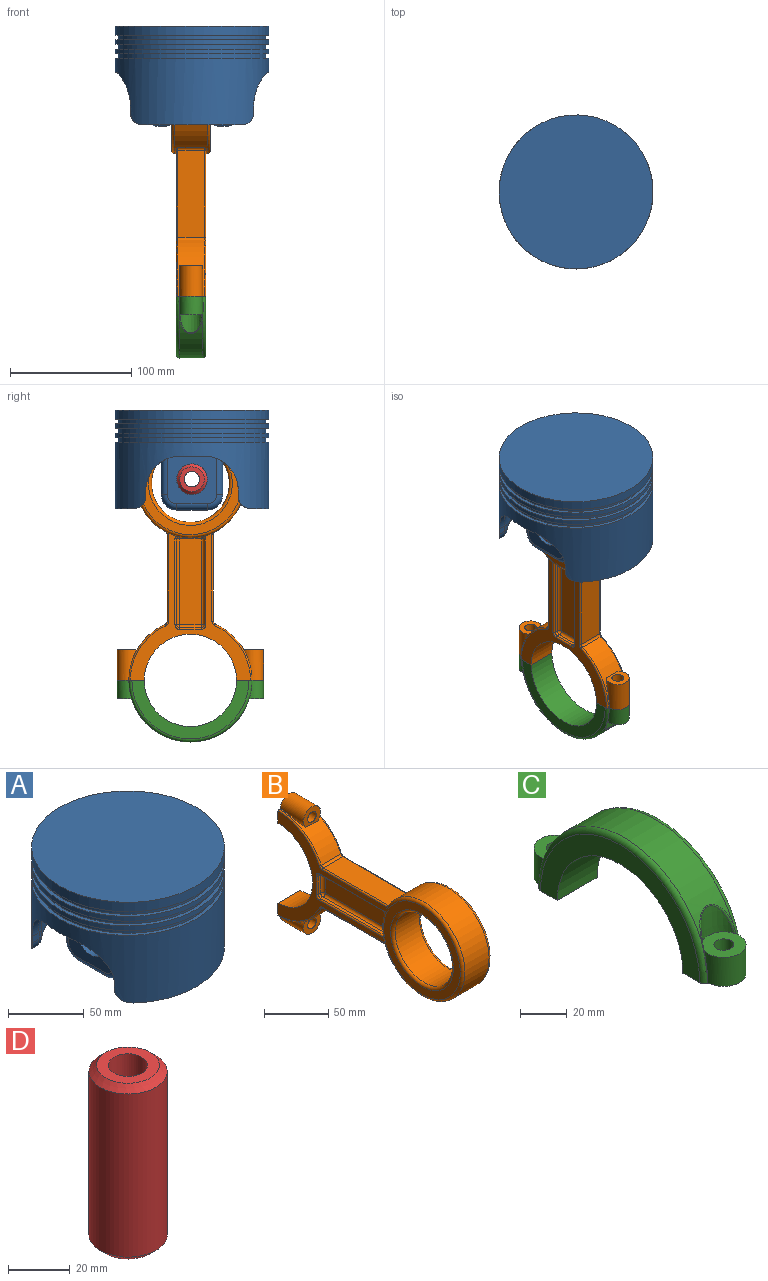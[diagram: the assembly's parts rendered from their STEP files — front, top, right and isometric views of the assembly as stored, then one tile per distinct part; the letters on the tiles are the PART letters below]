
ASSEMBLY  parts=4 mates=7
PART A: 84 faces, bbox 133.2x142.2x83.5 mm
  f0: plane 114.3x114.3mm, normal (0,0,-1), area 8373.3mm2, adj f1,f28,f29,f30,f31,f33,f34,f35
  f1: cylinder r=57.15mm len=114.3mm, axis (0,0,-1), area 14043.6mm2, adj f0,f68,f69,f70,f71,f72,f73,f74
  f2: plane 82.91x15.4mm, normal (0,0,-1), area 118.5mm2, adj f3,f44,f47,f68
  f3: cylinder r=63.5mm len=127mm, axis (0,0,-1), area 15403.3mm2, adj f2,f16,f17,f18,f19,f20,f21,f22
  f4: cylinder r=63.5mm len=127mm, axis (0,0,-1), area 1520.1mm2, adj f13,f14
  f5: cylinder r=63.5mm len=127mm, axis (0,0,-1), area 1520.1mm2, adj f8,f11
  f6: plane 127x127mm, normal (0,0,-1), area 993.1mm2, adj f7,f10
  f7: cylinder r=60.96mm len=121.92mm, axis (0,0,-1), area 1459.3mm2, adj f6,f8
  f8: plane 127x127mm, normal (0,0,1), area 993.1mm2, adj f5,f7
  f9: plane 127x127mm, normal (0,0,1), area 12667.7mm2, adj f10
  f10: cylinder r=63.5mm len=127mm, axis (0,0,-1), area 3040.2mm2, adj f6,f9
  f11: plane 127x127mm, normal (0,0,-1), area 993.1mm2, adj f5,f12
  f12: cylinder r=60.96mm len=121.92mm, axis (0,0,-1), area 1459.3mm2, adj f11,f13
  f13: plane 127x127mm, normal (0,0,1), area 993.1mm2, adj f4,f12
  f14: plane 127x127mm, normal (0,0,-1), area 993.1mm2, adj f4,f15
  f15: cylinder r=60.96mm len=121.92mm, axis (0,0,-1), area 1459.3mm2, adj f14,f16
  f16: plane 127x127mm, normal (0,0,1), area 993.1mm2, adj f3,f15
  f17: plane 82.91x15.4mm, normal (0,0,-1), area 118.5mm2, adj f3,f45,f46,f83
  f18: plane 6.02x5.18mm, normal (0,1,0), area 31.2mm2, adj f3,f25,f45,f79
  f19: plane 20.2x2.18mm, normal (0,0,-1), area 27.4mm2, adj f3,f24,f25,f75
  f20: plane 6.02x5.18mm, normal (0,-1,0), area 31.2mm2, adj f3,f24,f44,f71
  f21: plane 6.02x5.18mm, normal (0,-1,0), area 31.2mm2, adj f3,f26,f47,f72
  f22: plane 20.2x2.18mm, normal (0,0,-1), area 27.4mm2, adj f3,f26,f27,f76
  f23: plane 6.02x5.18mm, normal (0,1,0), area 31.2mm2, adj f3,f27,f46,f80
  f24: cylinder r=28mm len=28mm, axis (1,0,0), area 162.4mm2, adj f3,f19,f20,f73
  f25: cylinder r=28mm len=28mm, axis (-1,0,0), area 162.4mm2, adj f3,f18,f19,f77
  f26: cylinder r=28mm len=28mm, axis (1,0,0), area 162.4mm2, adj f3,f21,f22,f74
  f27: cylinder r=28mm len=28mm, axis (-1,0,0), area 162.4mm2, adj f3,f22,f23,f78
  f28: plane 58.5x40.8mm, normal (-1,0,0), area 1854.6mm2, adj f0,f39,f53,f54,f55,f56,f57
  f29: plane 50.8x9mm, normal (0,1,0), area 457.2mm2, adj f0,f42,f52,f57
  f30: plane 58.5x40.8mm, normal (1,0,0), area 1854.6mm2, adj f0,f39,f48,f49,f50,f51,f52
  f31: plane 50.8x9mm, normal (0,-1,0), area 457.2mm2, adj f0,f43,f48,f53
  f32: plane 25.4x9mm, normal (0,0,-1), area 228.6mm2, adj f42,f43,f50,f55
  f33: plane 58.5x40.8mm, normal (1,0,0), area 1854.6mm2, adj f0,f38,f58,f59,f60,f61,f62
  f34: plane 50.8x9mm, normal (0,-1,0), area 457.2mm2, adj f0,f41,f58,f63
  f35: plane 58.5x40.8mm, normal (-1,0,0), area 1854.6mm2, adj f0,f38,f63,f64,f65,f66,f67
  f36: plane 50.8x9mm, normal (0,1,0), area 457.2mm2, adj f0,f40,f62,f67
  f37: plane 25.4x9mm, normal (0,0,-1), area 228.6mm2, adj f40,f41,f60,f65
  f38: cylinder r=12.7mm len=25.4mm, axis (1,0,0), area 1516.1mm2, adj f33,f35
  f39: cylinder r=12.7mm len=25.4mm, axis (1,0,0), area 1516.1mm2, adj f28,f30
  f40: cylinder r=12.7mm len=12.7mm, axis (-1,0,0), area 179.5mm2, adj f36,f37,f61,f66
  f41: cylinder r=12.7mm len=12.7mm, axis (1,0,0), area 179.5mm2, adj f34,f37,f59,f64
  f42: cylinder r=12.7mm len=12.7mm, axis (-1,0,0), area 179.5mm2, adj f29,f32,f51,f56
  f43: cylinder r=12.7mm len=12.7mm, axis (1,0,0), area 179.5mm2, adj f31,f32,f49,f54
  f44: cylinder r=10mm len=11.44mm, axis (-1,0,0), area 75.1mm2, adj f2,f3,f20,f69
  f45: cylinder r=10mm len=11.44mm, axis (1,0,0), area 75.1mm2, adj f3,f17,f18,f81
  f46: cylinder r=10mm len=11.44mm, axis (1,0,0), area 75.1mm2, adj f3,f17,f23,f82
  f47: cylinder r=10mm len=11.44mm, axis (-1,0,0), area 75.1mm2, adj f2,f3,f21,f70
  f48: cylinder r=5mm len=50.8mm, axis (0,0,-1), area 399mm2, adj f0,f30,f31,f49
  f49: torus R=7.7mm, axis (-1,0,0), area 134.3mm2, adj f30,f43,f48,f50
  f50: cylinder r=5mm len=25.4mm, axis (0,1,0), area 199.5mm2, adj f30,f32,f49,f51
  f51: torus R=7.7mm, axis (-1,0,0), area 134.3mm2, adj f30,f42,f50,f52
  f52: cylinder r=5mm len=50.8mm, axis (0,0,1), area 399mm2, adj f0,f29,f30,f51
  f53: cylinder r=5mm len=50.8mm, axis (0,0,1), area 399mm2, adj f0,f28,f31,f54
  f54: torus R=7.7mm, axis (-1,0,0), area 134.3mm2, adj f28,f43,f53,f55
  f55: cylinder r=5mm len=25.4mm, axis (0,-1,0), area 199.5mm2, adj f28,f32,f54,f56
  f56: torus R=7.7mm, axis (-1,0,0), area 134.3mm2, adj f28,f42,f55,f57
  f57: cylinder r=5mm len=50.8mm, axis (0,0,-1), area 399mm2, adj f0,f28,f29,f56
  f58: cylinder r=5mm len=50.8mm, axis (0,0,1), area 399mm2, adj f0,f33,f34,f59
  f59: torus R=7.7mm, axis (-1,0,0), area 134.3mm2, adj f33,f41,f58,f60
  f60: cylinder r=5mm len=25.4mm, axis (0,1,0), area 199.5mm2, adj f33,f37,f59,f61
  f61: torus R=7.7mm, axis (-1,0,0), area 134.3mm2, adj f33,f40,f60,f62
  f62: cylinder r=5mm len=50.8mm, axis (0,0,-1), area 399mm2, adj f0,f33,f36,f61
  f63: cylinder r=5mm len=50.8mm, axis (0,0,-1), area 399mm2, adj f0,f34,f35,f64
  f64: torus R=7.7mm, axis (-1,0,0), area 134.3mm2, adj f35,f41,f63,f65
  f65: cylinder r=5mm len=25.4mm, axis (0,-1,0), area 199.5mm2, adj f35,f37,f64,f66
  f66: torus R=7.7mm, axis (-1,0,0), area 134.3mm2, adj f35,f40,f65,f67
  f67: cylinder r=5mm len=50.8mm, axis (0,0,1), area 399mm2, adj f0,f35,f36,f66
  f68: torus R=62.15mm, axis (0,0,1), area 635.2mm2, adj f1,f2,f69,f70
  f69: bspline ~12.39x11.8mm, area 72.5mm2, adj f1,f44,f68,f71
  f70: bspline ~12.39x11.8mm, area 72.5mm2, adj f1,f47,f68,f72
  f71: cylinder r=5mm len=5.18mm, axis (0,0,-1), area 20.8mm2, adj f1,f20,f69,f73
  f72: cylinder r=5mm len=5.18mm, axis (0,0,-1), area 20.8mm2, adj f1,f21,f70,f74
  f73: bspline ~36.14x33.41mm, area 287.9mm2, adj f1,f24,f71,f75
  f74: bspline ~36.14x33.41mm, area 287.9mm2, adj f1,f26,f72,f76
  f75: torus R=62.15mm, axis (0,0,1), area 151.2mm2, adj f1,f19,f73,f77
  f76: torus R=62.15mm, axis (0,0,1), area 151.2mm2, adj f1,f22,f74,f78
  f77: bspline ~36.14x33.41mm, area 287.9mm2, adj f1,f25,f75,f79
  f78: bspline ~36.14x33.41mm, area 287.9mm2, adj f1,f27,f76,f80
  f79: cylinder r=5mm len=5.18mm, axis (0,0,-1), area 20.8mm2, adj f1,f18,f77,f81
  f80: cylinder r=5mm len=5.18mm, axis (0,0,-1), area 20.8mm2, adj f1,f23,f78,f82
  f81: bspline ~12.39x11.8mm, area 72.5mm2, adj f1,f45,f79,f83
  f82: bspline ~12.39x11.8mm, area 72.5mm2, adj f1,f46,f80,f83
  f83: torus R=62.15mm, axis (0,0,1), area 635.2mm2, adj f1,f17,f81,f82
PART B: 93 faces, bbox 31.8x210.9x120.7 mm
  f0: plane 24.13x22.23mm, normal (0,1,0), area 377.1mm2, adj f1,f2,f11,f12,f16,f17,f88,f92
  f1: plane 121.49x99.1mm, normal (-1,0,0), area 2156.5mm2, adj f0,f4,f10,f11,f63,f64,f65,f66
  f2: cylinder r=50.8mm len=46.45mm, axis (-1,0,0), area 789.9mm2, adj f0,f17,f18,f42,f88,f92
  f3: cylinder r=32.04mm len=64.08mm, axis (-1,0,0), area 5370mm2, adj f44,f46
  f4: cylinder r=44.74mm len=89.48mm, axis (-1,0,0), area 6481.6mm2, adj f1,f12,f19,f30,f39,f40,f43,f45
  f5: plane 84.4x84.4mm, normal (1,0,0), area 1838mm2, adj f45,f46
  f6: plane 84.4x84.4mm, normal (-1,0,0), area 1838mm2, adj f43,f44
  f7: plane 71.63x21.63mm, normal (0,0,1), area 1549.2mm2, adj f39,f42,f86,f90
  f8: plane 71.63x21.63mm, normal (0,0,-1), area 1549.2mm2, adj f40,f41,f79,f82
  f9: cylinder r=50.8mm len=46.45mm, axis (-1,0,0), area 789.9mm2, adj f10,f13,f15,f41,f77,f84
  f10: plane 24.13x22.23mm, normal (0,1,0), area 377.1mm2, adj f1,f9,f11,f12,f14,f15,f77,f84
  f11: cylinder r=38.1mm len=76.2mm, axis (-1,0,0), area 2888.2mm2, adj f0,f1,f10,f12
  f12: plane 121.49x99.1mm, normal (1,0,0), area 2156.5mm2, adj f0,f4,f10,f11,f70,f71,f72,f73
  f13: plane 19.05x16.33mm, normal (0,-1,0), area 188.9mm2, adj f9,f14,f15
  f14: cylinder r=4.76mm len=25.4mm, axis (0,1,0), area 759.7mm2, adj f10,f13
  f15: cylinder r=9.53mm len=25.4mm, axis (0,1,0), area 876.8mm2, adj f9,f10,f13
  f16: cylinder r=4.76mm len=25.4mm, axis (0,1,0), area 759.7mm2, adj f0,f18
  f17: cylinder r=9.53mm len=25.4mm, axis (0,1,0), area 876.8mm2, adj f0,f2,f18
  f18: plane 19.05x16.33mm, normal (0,-1,0), area 188.9mm2, adj f2,f16,f17
  f19: plane 20.26x1.48mm, normal (-1,0,0), area 22mm2, adj f4,f20,f47,f49
  f20: plane 17.78x3.81mm, normal (0,1,0), area 67.7mm2, adj f19,f36,f47,f49
  f21: plane 70.87x2.54mm, normal (0,0,1), area 180mm2, adj f38,f49,f62,f75
  f22: plane 17.78x2.54mm, normal (0,-1,0), area 45.2mm2, adj f37,f60,f62,f73
  f23: plane 70.87x2.54mm, normal (0,0,-1), area 180mm2, adj f35,f47,f60,f71
  f24: plane 70.87x17.78mm, normal (1,0,0), area 1260.1mm2, adj f35,f36,f37,f38
  f25: plane 17.78x3.81mm, normal (0,1,0), area 67.7mm2, adj f30,f32,f53,f57
  f26: plane 70.87x2.54mm, normal (0,0,-1), area 180mm2, adj f31,f51,f53,f64
  f27: plane 17.78x2.54mm, normal (0,-1,0), area 45.2mm2, adj f33,f51,f55,f66
  f28: plane 70.87x2.54mm, normal (0,0,1), area 180mm2, adj f34,f55,f57,f68
  f29: plane 70.87x17.78mm, normal (-1,0,0), area 1260.1mm2, adj f31,f32,f33,f34
  f30: plane 20.26x1.48mm, normal (1,0,0), area 22mm2, adj f4,f25,f53,f57
  f31: cylinder r=2.54mm len=70.87mm, axis (0,1,0), area 282.8mm2, adj f26,f29,f52,f54
  f32: cylinder r=2.54mm len=17.78mm, axis (0,0,1), area 70.9mm2, adj f25,f29,f54,f58
  f33: cylinder r=2.54mm len=17.78mm, axis (0,0,-1), area 70.9mm2, adj f27,f29,f52,f56
  f34: cylinder r=2.54mm len=70.87mm, axis (0,-1,0), area 282.8mm2, adj f28,f29,f56,f58
  f35: cylinder r=2.54mm len=70.87mm, axis (0,-1,0), area 282.8mm2, adj f23,f24,f48,f59
  f36: cylinder r=2.54mm len=17.78mm, axis (0,0,-1), area 70.9mm2, adj f20,f24,f48,f50
  f37: cylinder r=2.54mm len=17.78mm, axis (0,0,1), area 70.9mm2, adj f22,f24,f59,f61
  f38: cylinder r=2.54mm len=70.87mm, axis (0,1,0), area 282.8mm2, adj f21,f24,f50,f61
  f39: cylinder r=2.54mm len=21.63mm, axis (-1,0,0), area 60.2mm2, adj f4,f7,f85,f89
  f40: cylinder r=2.54mm len=21.63mm, axis (-1,0,0), area 60.2mm2, adj f4,f8,f80,f81
  f41: cylinder r=2.54mm len=21.63mm, axis (-1,0,0), area 63.4mm2, adj f8,f9,f78,f83
  f42: cylinder r=2.54mm len=21.63mm, axis (-1,0,0), area 63.4mm2, adj f2,f7,f87,f91
  f43: torus R=42.2mm, axis (1,0,0), area 1098.4mm2, adj f4,f6
  f44: torus R=34.58mm, axis (1,0,0), area 826.3mm2, adj f3,f6
  f45: torus R=42.2mm, axis (1,0,0), area 1098.4mm2, adj f4,f5
  f46: torus R=34.58mm, axis (1,0,0), area 826.3mm2, adj f3,f5
  f47: cylinder r=2.54mm len=3.81mm, axis (1,0,0), area 11.8mm2, adj f4,f19,f20,f23,f48,f70
  f48: sphere r=2.54mm, area 10.1mm2, adj f35,f36,f47
  f49: cylinder r=2.54mm len=3.81mm, axis (-1,0,0), area 11.8mm2, adj f4,f19,f20,f21,f50,f76
  f50: sphere r=2.54mm, area 10.1mm2, adj f36,f38,f49
  f51: cylinder r=2.54mm len=2.54mm, axis (1,0,0), area 10.1mm2, adj f26,f27,f52,f65
  f52: sphere r=2.54mm, area 10.1mm2, adj f31,f33,f51
  f53: cylinder r=2.54mm len=3.81mm, axis (-1,0,0), area 11.8mm2, adj f4,f25,f26,f30,f54,f63
  f54: sphere r=2.54mm, area 10.1mm2, adj f31,f32,f53
  f55: cylinder r=2.54mm len=2.54mm, axis (-1,0,0), area 10.1mm2, adj f27,f28,f56,f67
  f56: sphere r=2.54mm, area 10.1mm2, adj f33,f34,f55
  f57: cylinder r=2.54mm len=3.81mm, axis (1,0,0), area 11.8mm2, adj f4,f25,f28,f30,f58,f69
  f58: sphere r=2.54mm, area 10.1mm2, adj f32,f34,f57
  f59: sphere r=2.54mm, area 10.1mm2, adj f35,f37,f60
  f60: cylinder r=2.54mm len=2.54mm, axis (-1,0,0), area 10.1mm2, adj f22,f23,f59,f72
  f61: sphere r=2.54mm, area 10.1mm2, adj f37,f38,f62
  f62: cylinder r=2.54mm len=2.54mm, axis (1,0,0), area 10.1mm2, adj f21,f22,f61,f74
  f63: torus R=3.81mm, axis (1,0,0), area 5.5mm2, adj f1,f4,f53,f64
  f64: cylinder r=1.27mm len=70.87mm, axis (0,1,0), area 141.4mm2, adj f1,f26,f63,f65
  f65: torus R=3.81mm, axis (1,0,0), area 9.4mm2, adj f1,f51,f64,f66
  f66: cylinder r=1.27mm len=17.78mm, axis (0,0,-1), area 35.5mm2, adj f1,f27,f65,f67
  f67: torus R=3.81mm, axis (1,0,0), area 9.4mm2, adj f1,f55,f66,f68
  f68: cylinder r=1.27mm len=70.87mm, axis (0,-1,0), area 141.4mm2, adj f1,f28,f67,f69
  f69: torus R=3.81mm, axis (1,0,0), area 5.5mm2, adj f1,f4,f57,f68
  f70: torus R=3.81mm, axis (1,0,0), area 5.5mm2, adj f4,f12,f47,f71
  f71: cylinder r=1.27mm len=70.87mm, axis (0,1,0), area 141.4mm2, adj f12,f23,f70,f72
  f72: torus R=3.81mm, axis (1,0,0), area 9.4mm2, adj f12,f60,f71,f73
  f73: cylinder r=1.27mm len=17.78mm, axis (0,0,-1), area 35.5mm2, adj f12,f22,f72,f74
  f74: torus R=3.81mm, axis (1,0,0), area 9.4mm2, adj f12,f62,f73,f75
  f75: cylinder r=1.27mm len=70.87mm, axis (0,-1,0), area 141.4mm2, adj f12,f21,f74,f76
  f76: torus R=3.81mm, axis (1,0,0), area 5.5mm2, adj f4,f12,f49,f75
  f77: torus R=49.55mm, axis (1,0,0), area 114.1mm2, adj f1,f9,f10,f78
  f78: torus R=3.79mm, axis (1,0,0), area 6.8mm2, adj f1,f41,f77,f79
  f79: cylinder r=1.25mm len=71.63mm, axis (0,1,0), area 140.6mm2, adj f1,f8,f78,f80
  f80: torus R=3.79mm, axis (1,0,0), area 3.6mm2, adj f1,f4,f40,f79
  f81: torus R=3.79mm, axis (1,0,0), area 3.6mm2, adj f4,f12,f40,f82
  f82: cylinder r=1.25mm len=71.63mm, axis (0,-1,0), area 140.6mm2, adj f8,f12,f81,f83
  f83: torus R=3.79mm, axis (1,0,0), area 6.8mm2, adj f12,f41,f82,f84
  f84: torus R=49.55mm, axis (1,0,0), area 114.1mm2, adj f9,f10,f12,f83
  f85: torus R=3.79mm, axis (1,0,0), area 3.6mm2, adj f4,f12,f39,f86
  f86: cylinder r=1.25mm len=71.63mm, axis (0,1,0), area 140.6mm2, adj f7,f12,f85,f87
  f87: torus R=3.79mm, axis (1,0,0), area 6.8mm2, adj f12,f42,f86,f88
  f88: torus R=49.55mm, axis (1,0,0), area 114.1mm2, adj f0,f2,f12,f87
  f89: torus R=3.79mm, axis (1,0,0), area 3.6mm2, adj f1,f4,f39,f90
  f90: cylinder r=1.25mm len=71.63mm, axis (0,-1,0), area 140.6mm2, adj f1,f7,f89,f91
  f91: torus R=3.79mm, axis (1,0,0), area 6.8mm2, adj f1,f42,f90,f92
  f92: torus R=49.55mm, axis (1,0,0), area 114.1mm2, adj f0,f1,f2,f91
PART C: 22 faces, bbox 24.1x120.7x56.9 mm
  f0: cylinder r=50.8mm len=93.89mm, axis (-1,0,0), area 1911.8mm2, adj f18,f19,f20,f21
  f1: plane 24.13x22.23mm, normal (0,0,-1), area 303.2mm2, adj f2,f4,f5,f9,f17,f18,f19,f20
  f2: cylinder r=38.1mm len=76.2mm, axis (-1,0,0), area 2888.2mm2, adj f1,f3,f4,f5
  f3: plane 24.13x22.23mm, normal (0,0,-1), area 303.2mm2, adj f2,f4,f5,f7,f14,f18,f19,f21
  f4: plane 96.52x48.26mm, normal (1,0,0), area 1378.2mm2, adj f1,f2,f3,f19
  f5: plane 96.52x48.26mm, normal (-1,0,0), area 1378.2mm2, adj f1,f2,f3,f18
  f6: plane 19.05x19.05mm, normal (0,0,1), area 229.2mm2, adj f7,f10,f12
  f7: cylinder r=9.53mm len=19.05mm, axis (0,0,-1), area 505.2mm2, adj f3,f6,f21
  f8: plane 19.05x19.05mm, normal (0,0,1), area 229.2mm2, adj f9,f11,f15
  f9: cylinder r=9.53mm len=19.05mm, axis (0,0,-1), area 505.2mm2, adj f1,f8,f20
  f10: cone r=9.53mm half-angle=2deg, axis (0,0,1), area 250.1mm2, adj f6,f21
  f11: cone r=9.53mm half-angle=2deg, axis (0,0,1), area 250.1mm2, adj f8,f20
  f12: cylinder r=4.22mm len=8.43mm, axis (0,0,-1), area 193.7mm2, adj f6,f13
  f13: plane 13.49x13.49mm, normal (0,0,-1), area 87.2mm2, adj f12,f14
  f14: cylinder r=6.75mm len=13.49mm, axis (0,0,-1), area 336.5mm2, adj f3,f13
  f15: cylinder r=4.22mm len=8.43mm, axis (0,0,-1), area 193.7mm2, adj f8,f16
  f16: plane 13.49x13.49mm, normal (0,0,-1), area 87.2mm2, adj f15,f17
  f17: cylinder r=6.75mm len=13.49mm, axis (0,0,-1), area 336.5mm2, adj f1,f16
  f18: torus R=48.26mm, axis (1,0,0), area 613.1mm2, adj f0,f1,f3,f5,f20,f21
  f19: torus R=48.26mm, axis (1,0,0), area 613.1mm2, adj f0,f1,f3,f4,f20,f21
  f20: bspline ~32.54x20.29mm, area 53.3mm2, adj f0,f1,f9,f11,f18,f19
  f21: bspline ~32.54x20.29mm, area 53.3mm2, adj f0,f3,f7,f10,f18,f19
PART D: 6 faces, bbox 25.4x25.4x69.9 mm
  f0: cylinder r=6.35mm len=69.85mm, axis (0,0,-1), area 2786.9mm2, adj f2,f3
  f1: cylinder r=12.7mm len=64.85mm, axis (0,0,-1), area 5174.8mm2, adj f4,f5
  f2: plane 20.4x20.4mm, normal (0,0,1), area 200.2mm2, adj f0,f5
  f3: plane 20.4x20.4mm, normal (0,0,-1), area 200.2mm2, adj f0,f4
  f4: cone r=12.7mm half-angle=45deg, axis (0,0,1), area 254.4mm2, adj f1,f3
  f5: cone r=10.2mm half-angle=45deg, axis (0,0,-1), area 254.4mm2, adj f1,f2
PLACE A t=(-5.25,-23.93,9.9)mm fixed
PLACE B rot(axis=(-1,0,0),90deg) t=(-6.08,-22.6,-131.93)mm
PLACE C rot(axis=(0,-1,0),180deg) t=(-6.08,-22.6,-213.16)mm
PLACE D rot(axis=(-0.58,-0.58,0.58),120deg) t=(-4.52,-23.93,-47.2)mm
MATE slider A.f38 <-> D.f0  axis (1,0,0) through (-30.63,-23.93,-47.2)mm
MATE cylindrical B.f14 <-> C.f9  axis (0,0,-1) through (-6.08,-73.4,-213.16)mm
MATE cylindrical B.f16 <-> C.f7  axis (0,0,-1) through (-6.08,28.2,-213.16)mm
MATE parallel A.f38 <-> B.f3  axis (1,0,0) through (29.63,-23.93,-47.2)mm
MATE parallel A.f38 <-> B.f3  axis (1,0,0) through (29.63,-23.93,-47.2)mm
MATE parallel A.f38 <-> B.f3  axis (1,0,0) through (29.63,-23.93,-47.2)mm
MATE planar C.f9 <-> B.f14  axis (0,0,1) through (-6.08,-73.4,-213.16)mm
